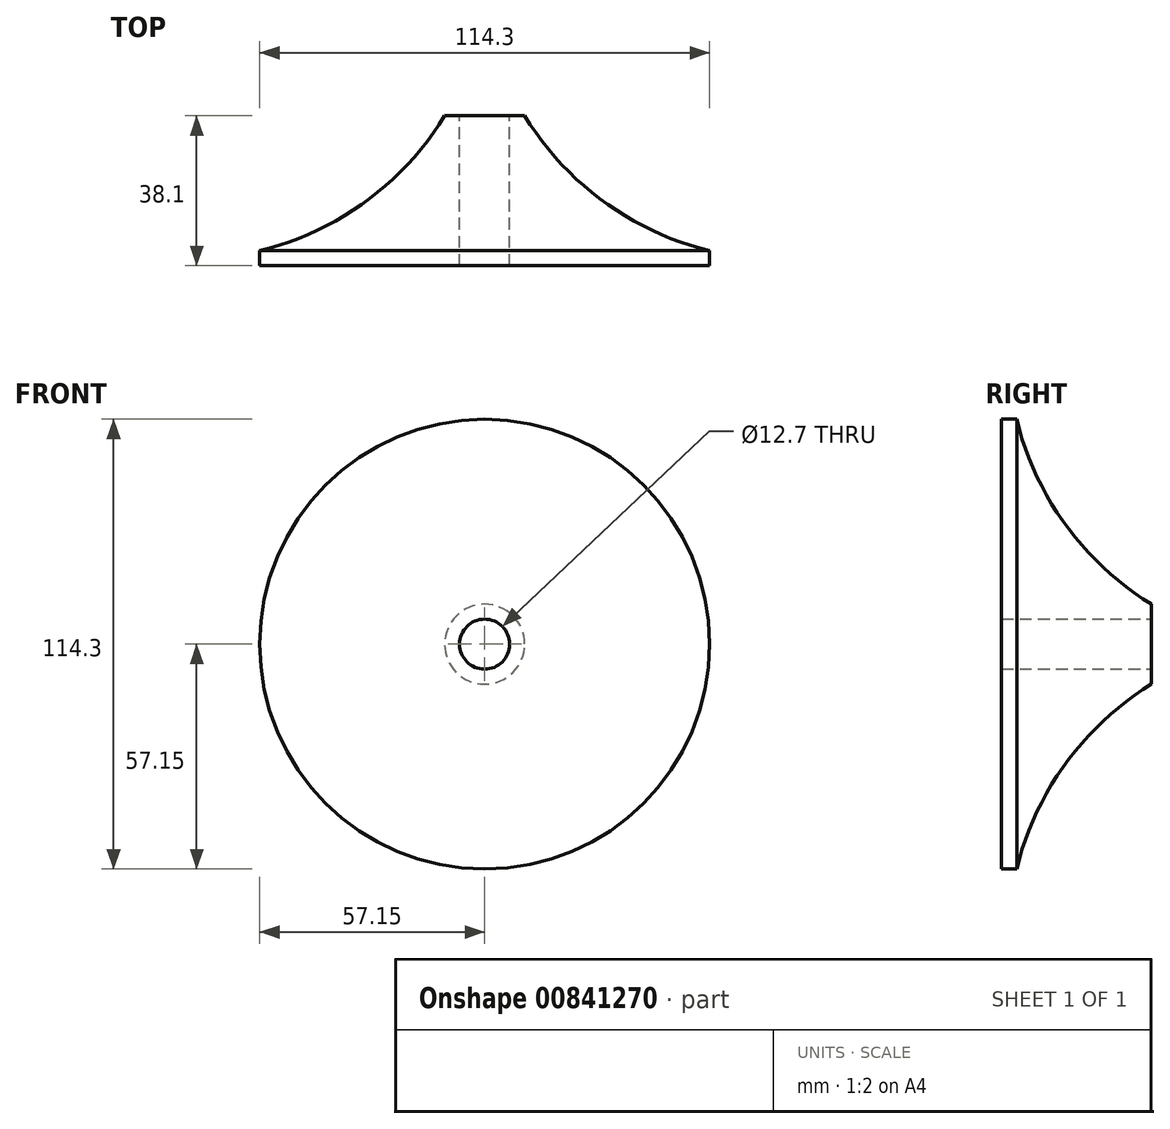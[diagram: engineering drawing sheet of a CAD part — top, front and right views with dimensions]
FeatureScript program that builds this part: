
annotation { "Feature Type Name" : "Feature", "Feature Type Description" : "" }
export const myFeature = defineFeature(function(context is Context, id is Id, definition is map)
    precondition{}
    {
        {
            var Q0;
            Q0=qCreatedBy(makeId("Top.planeOp"),FACE);
            var sketch = newSketch(context, id + "F0", { "sketchPlane" : qUnion([Q0])});
            skArc(sketch, "E0", {"start": v(-57.15, 3.64) * mm, "mid": v(-30.25, 16.13) * mm, "end": v(-10.16, 37.93) * mm});
            skLineSegment(sketch, "E1", {"start": v(-57.15, 3.64) * mm, "end": v(-57.15, -0.17) * mm});
            skLineSegment(sketch, "E2", {"start": v(-57.15, -0.17) * mm, "end": v(-6.35, -0.17) * mm});
            skLineSegment(sketch, "E3", {"start": v(-6.35, -0.17) * mm, "end": v(-6.35, 37.93) * mm});
            skLineSegment(sketch, "E4", {"start": v(-6.35, 37.93) * mm, "end": v(-10.16, 37.93) * mm});
            skLineSegment(sketch, "E5", {"start": v(0, 72.14) * mm, "end": v(0, -42.96) * mm, "construction": true});
            skSolve(sketch);
        }
        {
            var Q0;
            Q0 = qSketchRegion(id + "F0", true);
            var Q1;
            Q1=sQuery(id+"F0.wireOp",EDGE,"E5");
            revolve(context, id + "F1", {"surfaceOperationType" : NewSurfaceOperationType.NEW, "entities" : qUnion([Q0]), "axis" : qUnion([Q1]), "revolveType" : RevolveType.FULL});
        }
    });
